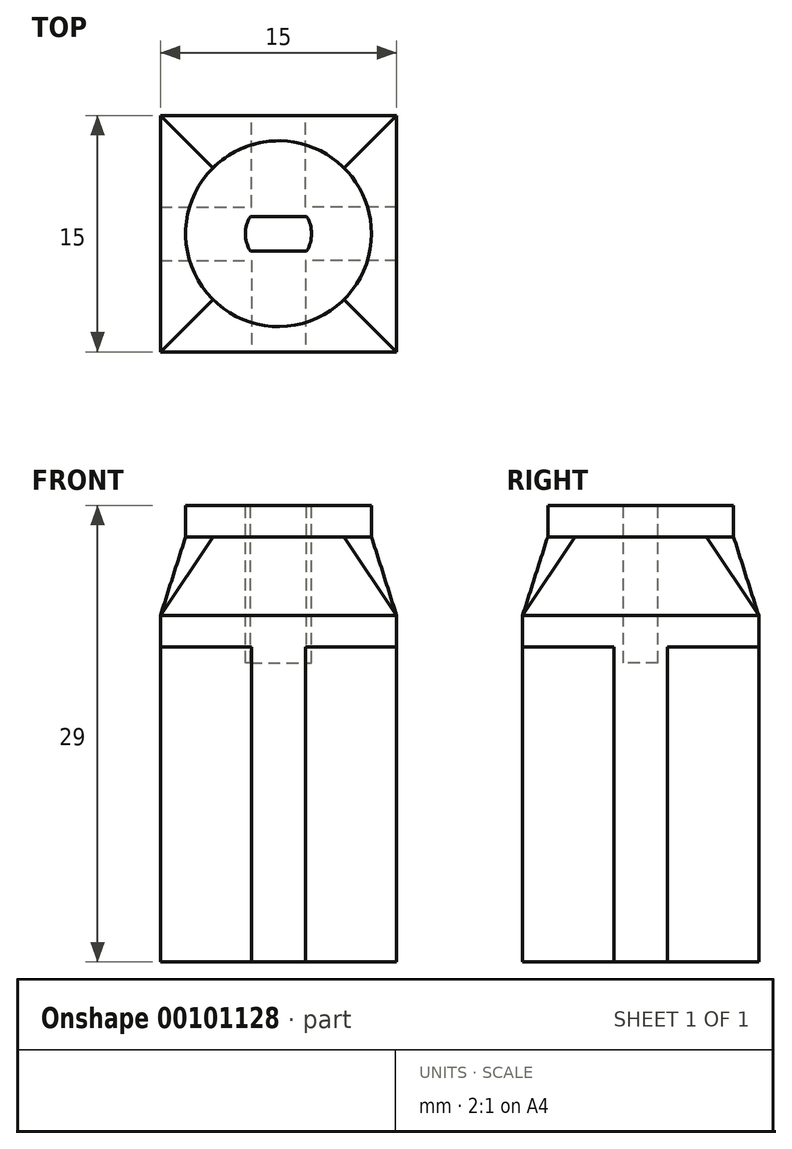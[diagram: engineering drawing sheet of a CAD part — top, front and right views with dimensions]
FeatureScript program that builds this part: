
annotation { "Feature Type Name" : "Feature", "Feature Type Description" : "" }
export const myFeature = defineFeature(function(context is Context, id is Id, definition is map)
    precondition{}
    {
        {
            var Q0;
            Q0=qCreatedBy(makeId("Top.planeOp"),FACE);
            var sketch = newSketch(context, id + "F0", { "sketchPlane" : qUnion([Q0])});
            skCircle(sketch, "E0", {"center": v(0, 0) * mm, "radius": 3.9 * mm});
            skCircle(sketch, "E1", {"center": v(0, 0) * mm, "radius": 5.9 * mm});
            skCircle(sketch, "E2", {"center": v(0, 0) * mm, "radius": 2.4 * mm});
            skSolve(sketch);
        }
        {
            var Q0;
            Q0=makeQuery(id+"F0.imprint","IMPRINT",FACE,{"disambiguationData":[TD([[makeQuery(id+"F0.imprint","IMPRINT",EDGE,{"derivedFrom":sQuery(id+"F0.wireOp",EDGE,"E0")}),1.0]])]});
            var Q1;
            Q1=makeQuery(id+"F0.imprint","IMPRINT",FACE,{"disambiguationData":[TD([[makeQuery(id+"F0.imprint","IMPRINT",EDGE,{"derivedFrom":sQuery(id+"F0.wireOp",EDGE,"E2")}),1.0]])]});
            extrude(context, id + "F1", {"entities" : qUnion([Q0, Q1]), "depth" : 2 * mm});
        }
        {
            var Q0;
            Q0=makeQuery(id+"F0.imprint","IMPRINT",FACE,{"disambiguationData":[TD([[makeQuery(id+"F0.imprint","IMPRINT",EDGE,{"derivedFrom":sQuery(id+"F0.wireOp",EDGE,"E0")}),-1.0]])]});
            extrude(context, id + "F2", {"entities" : qUnion([Q0]), "operationType" : NewBodyOperationType.ADD, "depth" : 2 * mm});
        }
        {
            var Q0;
            Q0=makeQuery(id+"F0.imprint","IMPRINT",FACE,{"disambiguationData":[TD([[makeQuery(id+"F0.imprint","IMPRINT",EDGE,{"derivedFrom":sQuery(id+"F0.wireOp",EDGE,"E0")}),-1.0]])]});
            cPlane(context, id + "F3", {"entities" : qUnion([Q0]), "cplaneType" : CPlaneType.OFFSET, "offset" : 5 * mm, "oppositeDirection" : true, "width" : 150 * mm, "height" : 150 * mm});
        }
        {
            var Q0;
            Q0=qCreatedBy(id+"F3.planeOp",FACE);
            var sketch = newSketch(context, id + "F4", { "sketchPlane" : qUnion([Q0])});
            skLineSegment(sketch, "E3.bottom", {"start": v(-7.5, -7.5) * mm, "end": v(7.5, -7.5) * mm});
            skLineSegment(sketch, "E3.top", {"start": v(-7.5, 7.5) * mm, "end": v(7.5, 7.5) * mm});
            skLineSegment(sketch, "E3.left", {"start": v(-7.5, -7.5) * mm, "end": v(-7.5, 7.5) * mm});
            skLineSegment(sketch, "E3.right", {"start": v(7.5, -7.5) * mm, "end": v(7.5, 7.5) * mm});
            skPoint(sketch, "E3.middle", {"position": v(0, 0) * mm});
            skSolve(sketch);
        }
        {
            var Q0;
            Q0=makeQuery(id+"F4.imprint","IMPRINT",FACE,{"disambiguationData":[TD([[makeQuery(id+"F4.imprint","IMPRINT",EDGE,{"derivedFrom":sQuery(id+"F4.wireOp",EDGE,"E3.bottom")}),1.0]])]});
            extrude(context, id + "F5", {"entities" : qUnion([Q0]), "oppositeDirection" : true, "depth" : 2 * mm});
        }
        {
            var Q1;
            {var subQ0=sQuery(id+"F0.wireOp",EDGE,"E0");Q1=makeQuery(id+"F2.boolean.opBoolean","MERGE",FACE,{"derivedFrom":[makeQuery(id+"F1.opExtrude","CAP_FACE",FACE,{"disambiguationData":[OSD([subQ0])],"isStart":true}),makeQuery(id+"F2.opExtrude","CAP_FACE",FACE,{"disambiguationData":[OSD([subQ0,sQuery(id+"F0.wireOp",EDGE,"E1")])],"isStart":true})]});}
            var Q2;
            Q2=makeQuery(id+"F5.opExtrude","CAP_FACE",FACE,{"disambiguationData":[OSD([sQuery(id+"F4.wireOp",EDGE,"E3.bottom"),sQuery(id+"F4.wireOp",EDGE,"E3.top"),sQuery(id+"F4.wireOp",EDGE,"E3.left"),sQuery(id+"F4.wireOp",EDGE,"E3.right")])],"isStart":true});
            loft(context, id + "F6", {"operationType" : NewBodyOperationType.ADD, "sheetProfilesArray" : [{ "sheetProfileEntities" : qUnion([Q1]) }, { "sheetProfileEntities" : qUnion([Q2]) }]});
        }
        {
            var Q0;
            Q0=makeQuery(id+"F5.opExtrude","CAP_FACE",FACE,{"disambiguationData":[OSD([sQuery(id+"F4.wireOp",EDGE,"E3.bottom"),sQuery(id+"F4.wireOp",EDGE,"E3.top"),sQuery(id+"F4.wireOp",EDGE,"E3.left"),sQuery(id+"F4.wireOp",EDGE,"E3.right")])],"isStart":false});
            var sketch = newSketch(context, id + "F7", { "sketchPlane" : qUnion([Q0])});
            skPoint(sketch, "E4", {"position": v(-7.5, 0) * mm});
            skLineSegment(sketch, "E5", {"start": v(-7.5, -1.7) * mm, "end": v(-1.7, -1.7) * mm});
            skLineSegment(sketch, "E6", {"start": v(-1.7, -1.7) * mm, "end": v(-1.7, -7.5) * mm});
            skLineSegment(sketch, "E7.MirrorCS", {"start": v(1.7, -1.7) * mm, "end": v(1.7, -7.5) * mm});
            skLineSegment(sketch, "E8.MirrorCS", {"start": v(7.5, -1.7) * mm, "end": v(1.7, -1.7) * mm});
            skLineSegment(sketch, "E9.MirrorCS", {"start": v(-7.5, 1.7) * mm, "end": v(-1.7, 1.7) * mm});
            skLineSegment(sketch, "E10.MirrorCS", {"start": v(-1.7, 1.7) * mm, "end": v(-1.7, 7.5) * mm});
            skLineSegment(sketch, "E11.MirrorCS", {"start": v(1.7, 1.7) * mm, "end": v(1.7, 7.5) * mm});
            skLineSegment(sketch, "E12.MirrorCS", {"start": v(7.5, 1.7) * mm, "end": v(1.7, 1.7) * mm});
            skSolve(sketch);
        }
        {
            var Q0;
            {var subQ8=sQuery(id+"F7.wireOp",EDGE,"E5");Q0=makeQuery(id+"F7.imprint","IMPRINT",FACE,{"disambiguationData":[TD([[makeQuery(id+"F7.imprint","IMPRINT",EDGE,{"derivedFrom":subQ8}),1.0]])]});}
            extrude(context, id + "F8", {"entities" : qUnion([Q0]), "operationType" : NewBodyOperationType.ADD, "depth" : 20 * mm});
        }
        {
            var Q0;
            {var subQ0=sQuery(id+"F0.wireOp",EDGE,"E0");Q0=makeQuery(id+"F2.boolean.opBoolean","MERGE",FACE,{"derivedFrom":[makeQuery(id+"F1.opExtrude","CAP_FACE",FACE,{"disambiguationData":[OSD([subQ0])],"isStart":false}),makeQuery(id+"F2.opExtrude","CAP_FACE",FACE,{"disambiguationData":[OSD([subQ0,sQuery(id+"F0.wireOp",EDGE,"E1")])],"isStart":false})]});}
            var sketch = newSketch(context, id + "F9", { "sketchPlane" : qUnion([Q0])});
            skCircle(sketch, "E13", {"center": v(0, 0) * mm, "radius": 2.1 * mm});
            skLineSegment(sketch, "E14", {"start": v(-1.79, 1.1) * mm, "end": v(1.79, 1.1) * mm});
            skLineSegment(sketch, "E15", {"start": v(-1.79, -1.1) * mm, "end": v(1.79, -1.1) * mm});
            skSolve(sketch);
        }
        {
            var Q0;
            {var subQ0=sQuery(id+"F9.wireOp",EDGE,"E14");Q0=makeQuery(id+"F9.imprint","IMPRINT",FACE,{"disambiguationData":[TD([[makeQuery(id+"F9.imprint","IMPRINT",EDGE,{"derivedFrom":subQ0}),-1.0]])]});}
            extrude(context, id + "F10", {"entities" : qUnion([Q0]), "operationType" : NewBodyOperationType.REMOVE, "oppositeDirection" : true, "depth" : 10 * mm});
        }
    });
